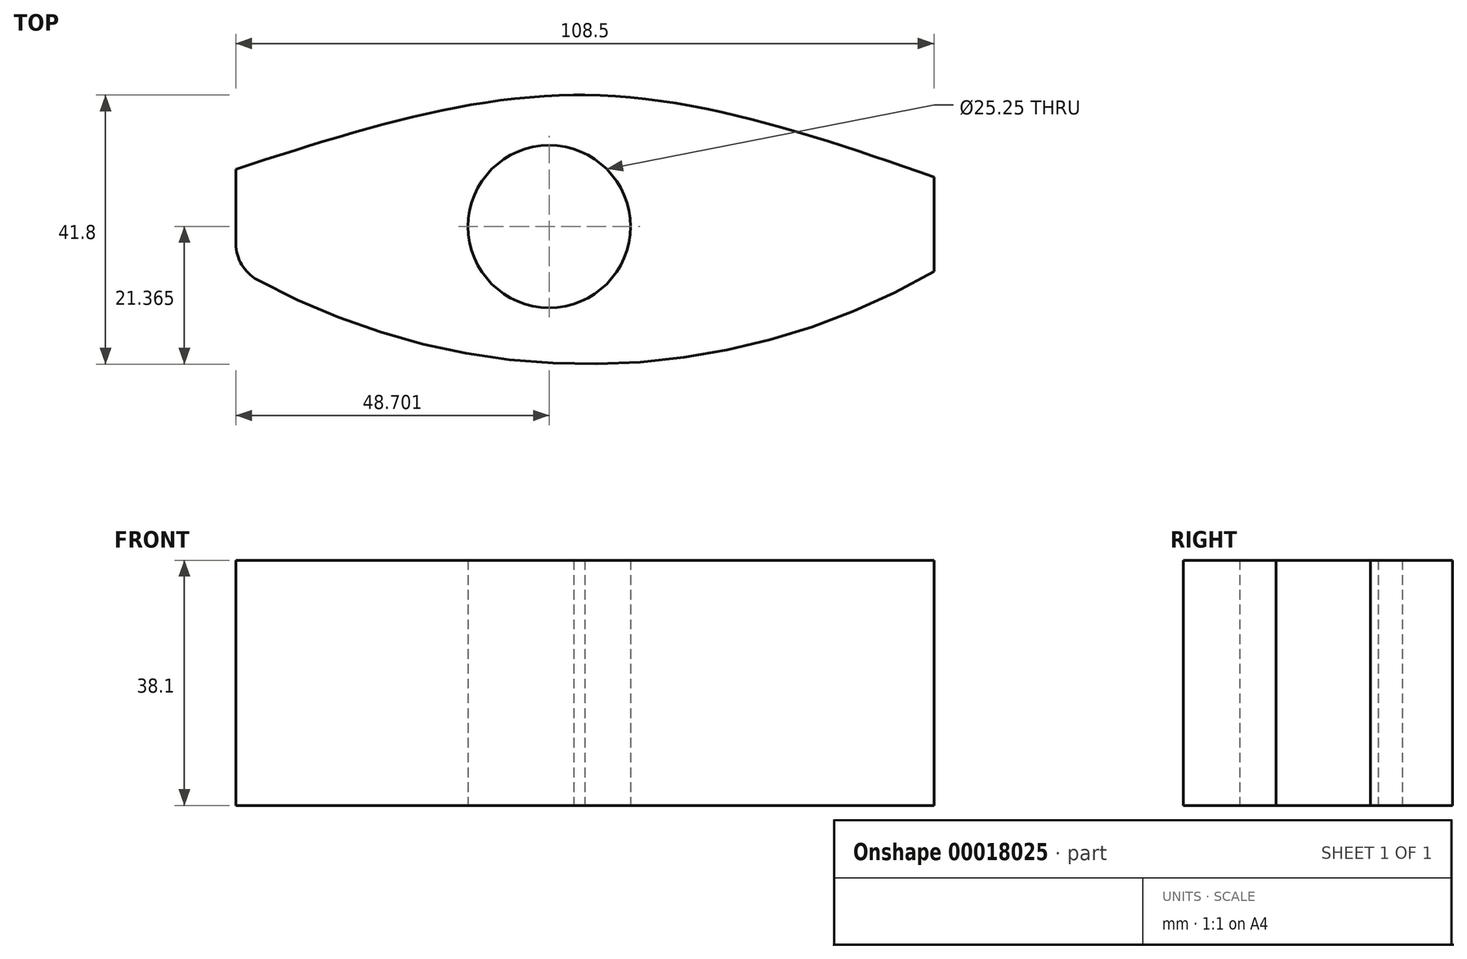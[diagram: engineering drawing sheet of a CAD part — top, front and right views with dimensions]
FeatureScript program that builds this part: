
annotation { "Feature Type Name" : "Feature", "Feature Type Description" : "" }
export const myFeature = defineFeature(function(context is Context, id is Id, definition is map)
    precondition{}
    {
        {
            var Q0;
            Q0=qCreatedBy(makeId("Top.planeOp"),FACE);
            var sketch = newSketch(context, id + "F0", { "sketchPlane" : qUnion([Q0])});
            skLineSegment(sketch, "E0.bottom", {"start": v(9.47, 54.25) * mm, "end": v(11.21, 54.25) * mm});
            skLineSegment(sketch, "E0.left", {"start": v(-43.04, 42.73) * mm, "end": v(-43.04, 31.12) * mm});
            skLineSegment(sketch, "E0.right", {"start": v(65.46, 41.52) * mm, "end": v(65.46, 26.82) * mm});
            skFitSpline(sketch, "E1", {"points": [v(-43.04, 42.73) * mm, v(11.21, 54.25) * mm, v(65.46, 41.52) * mm], "startDerivative": vector(108.7, 35.17) * mm, "endDerivative": vector(108.3, -37.56) * mm});
            skPoint(sketch, "E2.orphan", {"position": v(-43.04, 54.25) * mm});
            skPoint(sketch, "E3.orphan", {"position": v(65.46, 54.25) * mm});
            skArc(sketch, "E4", {"start": v(-39.72, 25.55) * mm, "mid": v(13.04, 12.45) * mm, "end": v(65.46, 26.82) * mm});
            skPoint(sketch, "E0.top.start.orphan", {"position": v(-43.04, 12.12) * mm});
            skPoint(sketch, "E5.orphan", {"position": v(65.46, 12.12) * mm});
            skPoint(sketch, "E6.visualSharp", {"position": v(-43.04, 27.43) * mm});
            skArc(sketch, "E6.filletArc", {"start": v(-43.04, 31.12) * mm, "mid": v(-42.14, 27.88) * mm, "end": v(-39.72, 25.55) * mm});
            skCircle(sketch, "E7", {"center": v(5.66, 33.82) * mm, "radius": 12.62 * mm});
            skSolve(sketch);
        }
        {
            var Q0;
            {var subQ2=sQuery(id+"F0.wireOp",EDGE,"E0.bottom");Q0=makeQuery(id+"F0.imprint","IMPRINT",FACE,{"disambiguationData":[TD([[makeQuery(id+"F0.imprint","IMPRINT",EDGE,{"derivedFrom":subQ2}),-1.0]])]});}
            extrude(context, id + "F1", {"entities" : qUnion([Q0]), "depth" : 38.1 * mm});
        }
    });
